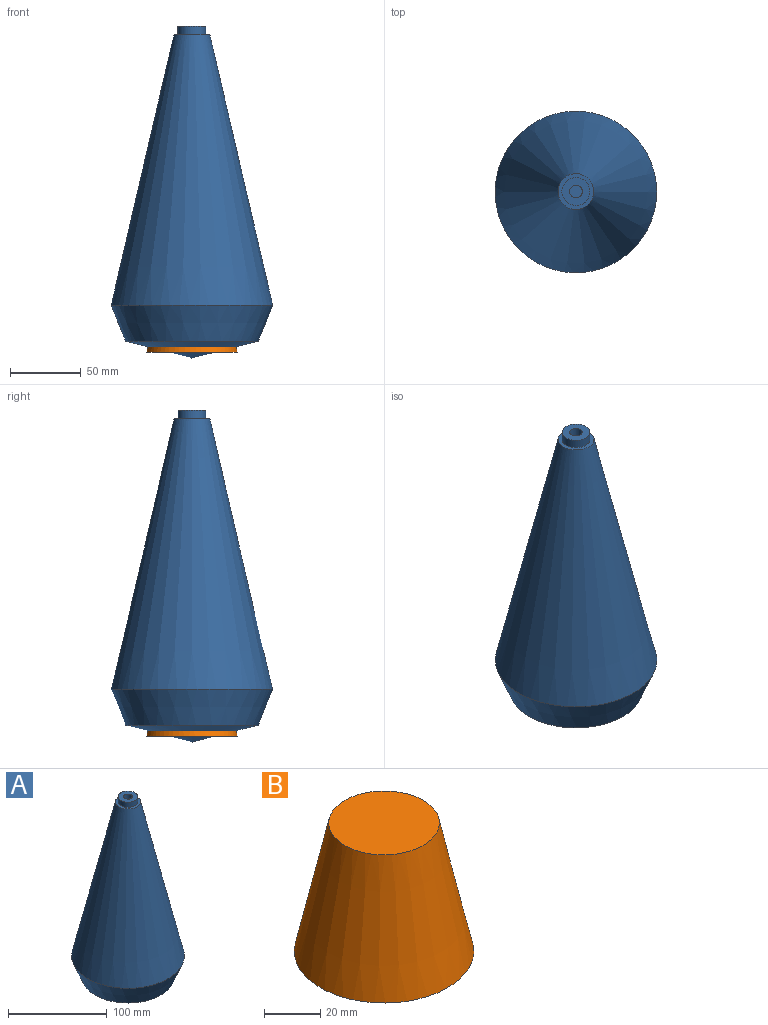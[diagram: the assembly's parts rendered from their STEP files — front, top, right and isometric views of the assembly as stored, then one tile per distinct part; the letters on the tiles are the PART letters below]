
ASSEMBLY  parts=2 mates=1
PART A: 12 faces, bbox 114.3x114.3x235 mm
  f0: cone r=46.94mm half-angle=75.7deg, axis (0,0,1), area 7143.1mm2, adj f1
  f1: cone r=57.15mm half-angle=21.9deg, axis (0,0,1), area 8951.9mm2, adj f0,f2
  f2: cone r=12.7mm half-angle=13.1deg, axis (0,0,-1), area 43089.1mm2, adj f1,f3
  f3: plane 25.4x25.4mm, normal (0,0,1), area 200mm2, adj f2,f5
  f4: cylinder r=4.45mm len=8.89mm, axis (0,0,-1), area 177.3mm2, adj f6,f7
  f5: cylinder r=9.88mm len=19.76mm, axis (0,0,-1), area 394.2mm2, adj f3,f6
  f6: plane 19.76x19.76mm, normal (0,0,1), area 244.6mm2, adj f4,f5
  f7: plane 8.89x8.89mm, normal (0,0,1), area 62.1mm2, adj f4
  f8: cone r=8.26mm half-angle=13.1deg, axis (0,0,-1), area 35736.7mm2, adj f9,f11
  f9: cone r=51.41mm half-angle=22.6deg, axis (0,0,1), area 6630.8mm2, adj f8,f10
  f10: cone r=42.82mm half-angle=75.7deg, axis (0,0,1), area 5942.3mm2, adj f9
  f11: plane 16.52x16.52mm, normal (0,0,-1), area 214.4mm2, adj f8
PART B: 5 faces, bbox 64x64x56 mm
  f0: plane 39.48x39.48mm, normal (0,0,1), area 1223.9mm2, adj f4
  f1: plane 30.48x30.48mm, normal (0,0,-1), area 729.7mm2, adj f2
  f2: cone r=15.24mm half-angle=12.3deg, axis (0,0,-1), area 6733.4mm2, adj f1,f3
  f3: plane 63.99x63.99mm, normal (0,0,-1), area 1047.1mm2, adj f2,f4
  f4: cone r=19.74mm half-angle=12.3deg, axis (0,0,-1), area 9320.3mm2, adj f0,f3
PLACE A t=(11.59,-34.29,-165.45)mm
PLACE B t=(11.59,-34.29,-198.57)mm
MATE cylindrical B.f2 <-> A.f5  axis (0,0,-1) through (11.59,-34.29,-148.13)mm
